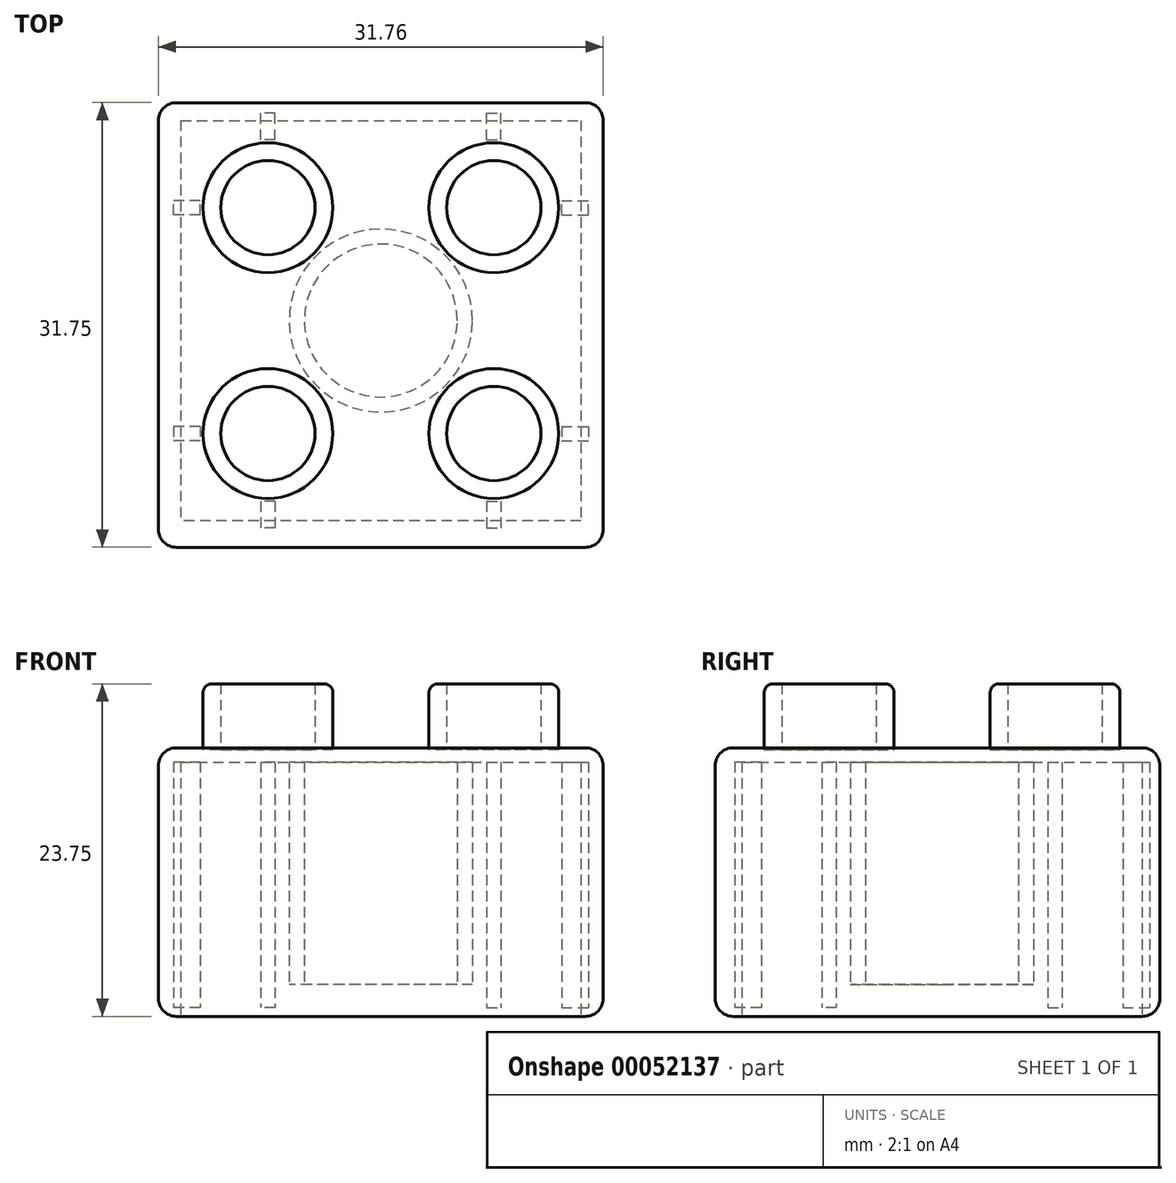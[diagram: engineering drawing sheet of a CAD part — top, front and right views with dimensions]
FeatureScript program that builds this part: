
annotation { "Feature Type Name" : "Feature", "Feature Type Description" : "" }
export const myFeature = defineFeature(function(context is Context, id is Id, definition is map)
    precondition{}
    {
        {
            var Q0;
            Q0=qCreatedBy(makeId("Top.planeOp"),FACE);
            var sketch = newSketch(context, id + "F0", { "sketchPlane" : qUnion([Q0])});
            skPoint(sketch, "E0", {"position": v(0, 16.87) * mm});
            skPoint(sketch, "E1", {"position": v(0, 15.88) * mm});
            skPoint(sketch, "E2", {"position": v(0, -14.88) * mm});
            skPoint(sketch, "E3", {"position": v(0, -15.88) * mm});
            skPoint(sketch, "E4", {"position": v(17.1, 0) * mm});
            skPoint(sketch, "E5", {"position": v(15.88, 0) * mm});
            skPoint(sketch, "E6", {"position": v(-15.88, 0) * mm});
            skPoint(sketch, "E7", {"position": v(15.64, 15.88) * mm});
            skPoint(sketch, "E8", {"position": v(15.88, 15.56) * mm});
            skPoint(sketch, "E9", {"position": v(-16.3, -15.88) * mm});
            skPoint(sketch, "E10", {"position": v(-15.88, -16.2) * mm});
            skLineSegment(sketch, "E11.bottom", {"start": v(-15.88, -16.2) * mm, "end": v(15.88, -16.2) * mm});
            skLineSegment(sketch, "E11.top", {"start": v(-15.88, 15.56) * mm, "end": v(15.88, 15.56) * mm});
            skLineSegment(sketch, "E11.left", {"start": v(-15.88, -16.2) * mm, "end": v(-15.88, 15.56) * mm});
            skLineSegment(sketch, "E11.right", {"start": v(15.88, -16.2) * mm, "end": v(15.88, 15.56) * mm});
            skSolve(sketch);
        }
        {
            var Q0;
            Q0=makeQuery(id+"F0.imprint","IMPRINT",FACE,{"disambiguationData":[TD([[makeQuery(id+"F0.imprint","IMPRINT",EDGE,{"derivedFrom":sQuery(id+"F0.wireOp",EDGE,"E11.bottom")}),1.0]])]});
            var sketch = newSketch(context, id + "F1", { "sketchPlane" : qUnion([Q0])});
            skPoint(sketch, "E12", {"position": v(14.77, 0) * mm});
            skPoint(sketch, "E13", {"position": v(14.29, 0) * mm});
            skPoint(sketch, "E14", {"position": v(-14.29, 0) * mm});
            skPoint(sketch, "E15", {"position": v(-14.29, -14.92) * mm});
            skPoint(sketch, "E16", {"position": v(-14.29, -14.29) * mm});
            skPoint(sketch, "E17", {"position": v(14.29, 14.33) * mm});
            skPoint(sketch, "E18", {"position": v(14.29, 14.29) * mm});
            skLineSegment(sketch, "E19.bottom", {"start": v(-14.29, -14.29) * mm, "end": v(14.29, -14.29) * mm});
            skLineSegment(sketch, "E19.top", {"start": v(-14.29, 14.29) * mm, "end": v(14.29, 14.29) * mm});
            skLineSegment(sketch, "E19.left", {"start": v(-14.29, -14.29) * mm, "end": v(-14.29, 14.29) * mm});
            skLineSegment(sketch, "E19.right", {"start": v(14.29, -14.29) * mm, "end": v(14.29, 14.29) * mm});
            skSolve(sketch);
        }
        {
            var Q0;
            Q0=makeQuery(id+"F1.imprint","IMPRINT",FACE,{"disambiguationData":[TD([[makeQuery(id+"F1.imprint","IMPRINT",EDGE,{"derivedFrom":sQuery(id+"F1.wireOp",EDGE,"E19.bottom")}),1.0]])]});
            var sketch = newSketch(context, id + "F2", { "sketchPlane" : qUnion([Q0])});
            skPoint(sketch, "E20", {"position": v(0, 0) * mm});
            skCircle(sketch, "E21", {"center": v(0, 0) * mm, "radius": 6.54 * mm});
            skSolve(sketch);
        }
        {
            var Q0;
            Q0=makeQuery(id+"F1.imprint","IMPRINT",FACE,{"disambiguationData":[TD([[makeQuery(id+"F1.imprint","IMPRINT",EDGE,{"derivedFrom":sQuery(id+"F1.wireOp",EDGE,"E19.bottom")}),1.0]])]});
            var sketch = newSketch(context, id + "F3", { "sketchPlane" : qUnion([Q0])});
            skPoint(sketch, "E22", {"position": v(0, 0) * mm});
            skCircle(sketch, "E23", {"center": v(0, 0) * mm, "radius": 5.46 * mm});
            skSolve(sketch);
        }
        {
            var Q0;
            Q0=makeQuery(id+"F1.imprint","IMPRINT",FACE,{"disambiguationData":[TD([[makeQuery(id+"F1.imprint","IMPRINT",EDGE,{"derivedFrom":sQuery(id+"F1.wireOp",EDGE,"E19.bottom")}),1.0]])]});
            var sketch = newSketch(context, id + "F4", { "sketchPlane" : qUnion([Q0])});
            skPoint(sketch, "E24", {"position": v(0, 1.02) * mm});
            skPoint(sketch, "E25", {"position": v(0, 0.95) * mm});
            skPoint(sketch, "E26", {"position": v(0, -0.95) * mm});
            skPoint(sketch, "E27", {"position": v(-0.23, 0) * mm});
            skPoint(sketch, "E28", {"position": v(-0.5, 0) * mm});
            skPoint(sketch, "E29", {"position": v(0.3, 0) * mm});
            skPoint(sketch, "E30", {"position": v(0.5, 0) * mm});
            skPoint(sketch, "E31", {"position": v(-0.5, -0.86) * mm});
            skPoint(sketch, "E32", {"position": v(-0.5, -0.95) * mm});
            skPoint(sketch, "E33", {"position": v(0.5, 0.95) * mm});
            skLineSegment(sketch, "E34.bottom", {"start": v(-0.5, -0.95) * mm, "end": v(0.5, -0.95) * mm});
            skLineSegment(sketch, "E34.top", {"start": v(-0.5, 0.95) * mm, "end": v(0.5, 0.95) * mm});
            skLineSegment(sketch, "E34.left", {"start": v(-0.5, -0.95) * mm, "end": v(-0.5, 0.95) * mm});
            skLineSegment(sketch, "E34.right", {"start": v(0.5, -0.95) * mm, "end": v(0.5, 0.95) * mm});
            skSolve(sketch);
        }
        {
            var Q0;
            Q0 = qSketchRegion(id + "F0", true);
            extrude(context, id + "F5", {"entities" : qUnion([Q0]), "depth" : 19.18 * mm});
        }
        {
            var Q0;
            Q0 = qSketchRegion(id + "F1", true);
            extrude(context, id + "F6", {"entities" : qUnion([Q0]), "operationType" : NewBodyOperationType.REMOVE, "depth" : 18.16 * mm, "hasSecondDirection" : true, "secondDirectionOppositeDirection" : true, "secondDirectionDepth" : 0.38 * mm});
        }
        {
            var Q0;
            Q0 = qSketchRegion(id + "F2", true);
            extrude(context, id + "F7", {"entities" : qUnion([Q0]), "operationType" : NewBodyOperationType.ADD, "depth" : 15.88 * mm});
        }
        {
            var Q0;
            Q0 = qSketchRegion(id + "F3", true);
            extrude(context, id + "F8", {"entities" : qUnion([Q0]), "operationType" : NewBodyOperationType.REMOVE, "depth" : 15.88 * mm, "hasSecondDirection" : true, "secondDirectionOppositeDirection" : true, "secondDirectionDepth" : 0.64 * mm});
        }
        {
            var Q0;
            Q0=makeQuery(id+"F7.opExtrude","SWEPT_BODY",BODY,{"disambiguationData":[OSD([sQuery(id+"F2.wireOp",EDGE,"E21")])]});
            transform(context, id + "F9", {"entities" : qUnion([Q0]), "transformType" : TransformType.TRANSLATION_3D, "dx" : 0 * mm, "dy" : 0 * mm, "dz" : 2.3 * mm, "makeCopy" : false});
        }
        {
            var Q0;
            Q0=makeQuery(id+"F4.imprint","IMPRINT",FACE,{"disambiguationData":[TD([[makeQuery(id+"F4.imprint","IMPRINT",EDGE,{"derivedFrom":sQuery(id+"F4.wireOp",EDGE,"E34.bottom")}),1.0]])]});
            extrude(context, id + "F10", {"entities" : qUnion([Q0]), "operationType" : NewBodyOperationType.ADD, "depth" : 17.53 * mm});
        }
        {
            var Q0;
            Q0=makeQuery(id+"F10.opExtrude","SWEPT_BODY",BODY,{"disambiguationData":[OSD([sQuery(id+"F4.wireOp",EDGE,"E34.bottom"),sQuery(id+"F4.wireOp",EDGE,"E34.top"),sQuery(id+"F4.wireOp",EDGE,"E34.left"),sQuery(id+"F4.wireOp",EDGE,"E34.right")])]});
            transform(context, id + "F11", {"entities" : qUnion([Q0]), "transformType" : TransformType.TRANSLATION_3D, "dx" : 8.06 * mm, "dy" : 13.86 * mm, "dz" : 0.64 * mm, "makeCopy" : false});
        }
        {
            var Q0;
            Q0=makeQuery(id+"F10.opExtrude","SWEPT_BODY",BODY,{"disambiguationData":[OSD([sQuery(id+"F4.wireOp",EDGE,"E34.bottom"),sQuery(id+"F4.wireOp",EDGE,"E34.top"),sQuery(id+"F4.wireOp",EDGE,"E34.left"),sQuery(id+"F4.wireOp",EDGE,"E34.right")])]});
            var Q1;
            Q1=qCreatedBy(makeId("Front.planeOp"),FACE);
            mirror(context, id + "F12", {"entities" : qUnion([Q0]), "mirrorPlane" : qUnion([Q1])});
        }
        {
            var Q0;
            Q0=makeQuery(id+"F12.opPattern","COPY",BODY,{"derivedFrom":makeQuery(id+"F10.opExtrude","SWEPT_BODY",BODY,{"disambiguationData":[OSD([sQuery(id+"F4.wireOp",EDGE,"E34.bottom"),sQuery(id+"F4.wireOp",EDGE,"E34.top"),sQuery(id+"F4.wireOp",EDGE,"E34.left"),sQuery(id+"F4.wireOp",EDGE,"E34.right")])]}),"instanceName":"1"});
            var Q1;
            Q1=makeQuery(id+"F10.opExtrude","SWEPT_BODY",BODY,{"disambiguationData":[OSD([sQuery(id+"F4.wireOp",EDGE,"E34.bottom"),sQuery(id+"F4.wireOp",EDGE,"E34.top"),sQuery(id+"F4.wireOp",EDGE,"E34.left"),sQuery(id+"F4.wireOp",EDGE,"E34.right")])]});
            var Q2;
            Q2=qCreatedBy(makeId("Right.planeOp"),FACE);
            mirror(context, id + "F13", {"entities" : qUnion([Q0, Q1]), "mirrorPlane" : qUnion([Q2])});
        }
        {
            var Q0;
            Q0=qCreatedBy(makeId("Front.planeOp"),FACE);
            var sketch = newSketch(context, id + "F14", { "sketchPlane" : qUnion([Q0])});
            skLineSegment(sketch, "E35", {"start": v(0, 40.9) * mm, "end": v(0, -32.36) * mm});
            skSolve(sketch);
        }
        {
            var Q0;
            Q0=makeQuery(id+"F12.opPattern","COPY",BODY,{"derivedFrom":makeQuery(id+"F10.opExtrude","SWEPT_BODY",BODY,{"disambiguationData":[OSD([sQuery(id+"F4.wireOp",EDGE,"E34.bottom"),sQuery(id+"F4.wireOp",EDGE,"E34.top"),sQuery(id+"F4.wireOp",EDGE,"E34.left"),sQuery(id+"F4.wireOp",EDGE,"E34.right")])]}),"instanceName":"1"});
            var Q1;
            Q1=makeQuery(id+"F13.opPattern","COPY",BODY,{"derivedFrom":makeQuery(id+"F12.opPattern","COPY",BODY,{"derivedFrom":makeQuery(id+"F10.opExtrude","SWEPT_BODY",BODY,{"disambiguationData":[OSD([sQuery(id+"F4.wireOp",EDGE,"E34.bottom"),sQuery(id+"F4.wireOp",EDGE,"E34.top"),sQuery(id+"F4.wireOp",EDGE,"E34.left"),sQuery(id+"F4.wireOp",EDGE,"E34.right")])]}),"instanceName":"1"}),"instanceName":"1"});
            var Q2;
            Q2=makeQuery(id+"F10.opExtrude","SWEPT_BODY",BODY,{"disambiguationData":[OSD([sQuery(id+"F4.wireOp",EDGE,"E34.bottom"),sQuery(id+"F4.wireOp",EDGE,"E34.top"),sQuery(id+"F4.wireOp",EDGE,"E34.left"),sQuery(id+"F4.wireOp",EDGE,"E34.right")])]});
            var Q3;
            Q3=makeQuery(id+"F13.opPattern","COPY",BODY,{"derivedFrom":makeQuery(id+"F10.opExtrude","SWEPT_BODY",BODY,{"disambiguationData":[OSD([sQuery(id+"F4.wireOp",EDGE,"E34.bottom"),sQuery(id+"F4.wireOp",EDGE,"E34.top"),sQuery(id+"F4.wireOp",EDGE,"E34.left"),sQuery(id+"F4.wireOp",EDGE,"E34.right")])]}),"instanceName":"1"});
            var Q4;
            Q4=sQuery(id+"F14.wireOp",EDGE,"E35");
            transform(context, id + "F15", {"entities" : qUnion([Q0, Q1, Q2, Q3]), "transformType" : TransformType.ROTATION, "transformAxis" : qUnion([Q4]), "angle" : 90 * degree, "makeCopy" : true});
        }
        {
            var Q0;
            Q0=qCreatedBy(makeId("Top.planeOp"),FACE);
            var sketch = newSketch(context, id + "F16", { "sketchPlane" : qUnion([Q0])});
            skCircle(sketch, "E36", {"center": v(0, 0) * mm, "radius": 4.64 * mm});
            skSolve(sketch);
        }
        {
            var Q0;
            Q0=qCreatedBy(makeId("Top.planeOp"),FACE);
            var sketch = newSketch(context, id + "F17", { "sketchPlane" : qUnion([Q0])});
            skCircle(sketch, "E37", {"center": v(0, 0) * mm, "radius": 3.37 * mm});
            skSolve(sketch);
        }
        {
            var Q0;
            Q0=makeQuery(id+"F16.imprint","IMPRINT",FACE,{"disambiguationData":[TD([[makeQuery(id+"F16.imprint","IMPRINT",EDGE,{"derivedFrom":sQuery(id+"F16.wireOp",EDGE,"E36")}),1.0]])]});
            extrude(context, id + "F18", {"entities" : qUnion([Q0]), "depth" : 4.7 * mm});
        }
        {
            var Q0;
            Q0=makeQuery(id+"F17.imprint","IMPRINT",FACE,{"disambiguationData":[TD([[makeQuery(id+"F17.imprint","IMPRINT",EDGE,{"derivedFrom":sQuery(id+"F17.wireOp",EDGE,"E37")}),1.0]])]});
            extrude(context, id + "F19", {"entities" : qUnion([Q0]), "operationType" : NewBodyOperationType.REMOVE, "depth" : 4.7 * mm});
        }
        {
            var Q0;
            Q0=makeQuery(id+"F18.opExtrude","SWEPT_BODY",BODY,{"disambiguationData":[OSD([sQuery(id+"F16.wireOp",EDGE,"E36")])]});
            transform(context, id + "F20", {"entities" : qUnion([Q0]), "transformType" : TransformType.TRANSLATION_3D, "dx" : 8.06 * mm, "dy" : 8.06 * mm, "dz" : 19.05 * mm, "makeCopy" : false});
        }
        {
            var Q0;
            Q0=makeQuery(id+"F18.opExtrude","SWEPT_BODY",BODY,{"disambiguationData":[OSD([sQuery(id+"F16.wireOp",EDGE,"E36")])]});
            var Q1;
            Q1=qCreatedBy(makeId("Front.planeOp"),FACE);
            mirror(context, id + "F21", {"entities" : qUnion([Q0]), "mirrorPlane" : qUnion([Q1])});
        }
        {
            var Q0;
            Q0=makeQuery(id+"F18.opExtrude","SWEPT_BODY",BODY,{"disambiguationData":[OSD([sQuery(id+"F16.wireOp",EDGE,"E36")])]});
            var Q1;
            Q1=makeQuery(id+"F21.opPattern","COPY",BODY,{"derivedFrom":makeQuery(id+"F18.opExtrude","SWEPT_BODY",BODY,{"disambiguationData":[OSD([sQuery(id+"F16.wireOp",EDGE,"E36")])]}),"instanceName":"1"});
            var Q2;
            Q2=qCreatedBy(makeId("Right.planeOp"),FACE);
            mirror(context, id + "F22", {"entities" : qUnion([Q0, Q1]), "mirrorPlane" : qUnion([Q2])});
        }
        {
            var Q0;
            Q0=makeQuery(id+"F5.opExtrude","CAP_EDGE",EDGE,{"disambiguationData":[OSD([sQuery(id+"F0.wireOp",EDGE,"E11.bottom")])],"isStart":false});
            var Q1;
            Q1=makeQuery(id+"F5.opExtrude","CAP_EDGE",EDGE,{"disambiguationData":[OSD([sQuery(id+"F0.wireOp",EDGE,"E11.left")])],"isStart":false});
            var Q2;
            Q2=makeQuery(id+"F5.opExtrude","CAP_EDGE",EDGE,{"disambiguationData":[OSD([sQuery(id+"F0.wireOp",EDGE,"E11.top")])],"isStart":false});
            var Q3;
            Q3=makeQuery(id+"F5.opExtrude","CAP_EDGE",EDGE,{"disambiguationData":[OSD([sQuery(id+"F0.wireOp",EDGE,"E11.right")])],"isStart":false});
            var Q4;
            Q4=makeQuery(id+"F5.opExtrude","SWEPT_EDGE",EDGE,{"disambiguationData":[OSD([sQuery(id+"F0.wireOp",EDGE,"E11.bottom"),sQuery(id+"F0.wireOp",EDGE,"E11.left")])]});
            var Q5;
            Q5=makeQuery(id+"F5.opExtrude","SWEPT_EDGE",EDGE,{"disambiguationData":[OSD([sQuery(id+"F0.wireOp",EDGE,"E11.bottom"),sQuery(id+"F0.wireOp",EDGE,"E11.right")])]});
            var Q6;
            Q6=makeQuery(id+"F5.opExtrude","SWEPT_EDGE",EDGE,{"disambiguationData":[OSD([sQuery(id+"F0.wireOp",EDGE,"E11.top"),sQuery(id+"F0.wireOp",EDGE,"E11.left")])]});
            var Q7;
            Q7=makeQuery(id+"F5.opExtrude","SWEPT_EDGE",EDGE,{"disambiguationData":[OSD([sQuery(id+"F0.wireOp",EDGE,"E11.top"),sQuery(id+"F0.wireOp",EDGE,"E11.right")])]});
            var Q8;
            Q8=makeQuery(id+"F5.opExtrude","CAP_EDGE",EDGE,{"disambiguationData":[OSD([sQuery(id+"F0.wireOp",EDGE,"E11.right")])],"isStart":true});
            var Q9;
            Q9=makeQuery(id+"F5.opExtrude","CAP_EDGE",EDGE,{"disambiguationData":[OSD([sQuery(id+"F0.wireOp",EDGE,"E11.bottom")])],"isStart":true});
            var Q10;
            Q10=makeQuery(id+"F5.opExtrude","CAP_EDGE",EDGE,{"disambiguationData":[OSD([sQuery(id+"F0.wireOp",EDGE,"E11.left")])],"isStart":true});
            var Q11;
            Q11=makeQuery(id+"F5.opExtrude","CAP_EDGE",EDGE,{"disambiguationData":[OSD([sQuery(id+"F0.wireOp",EDGE,"E11.top")])],"isStart":true});
            fillet(context, id + "F23", {"entities" : qUnion([Q0, Q1, Q2, Q3, Q4, Q5, Q6, Q7, Q8, Q9, Q10, Q11]), "radius" : 1.27 * mm, "tangentPropagation" : true, "allowEdgeOverflow" : false});
        }
        {
            var Q0;
            Q0=makeQuery(id+"F22.opPattern","COPY",EDGE,{"derivedFrom":makeQuery(id+"F18.opExtrude","CAP_EDGE",EDGE,{"disambiguationData":[OSD([sQuery(id+"F16.wireOp",EDGE,"E36")])],"isStart":false}),"instanceName":"1"});
            var Q1;
            Q1=makeQuery(id+"F18.opExtrude","CAP_EDGE",EDGE,{"disambiguationData":[OSD([sQuery(id+"F16.wireOp",EDGE,"E36")])],"isStart":false});
            var Q2;
            Q2=makeQuery(id+"F21.opPattern","COPY",EDGE,{"derivedFrom":makeQuery(id+"F18.opExtrude","CAP_EDGE",EDGE,{"disambiguationData":[OSD([sQuery(id+"F16.wireOp",EDGE,"E36")])],"isStart":false}),"instanceName":"1"});
            var Q3;
            Q3=makeQuery(id+"F22.opPattern","COPY",EDGE,{"derivedFrom":makeQuery(id+"F21.opPattern","COPY",EDGE,{"derivedFrom":makeQuery(id+"F18.opExtrude","CAP_EDGE",EDGE,{"disambiguationData":[OSD([sQuery(id+"F16.wireOp",EDGE,"E36")])],"isStart":false}),"instanceName":"1"}),"instanceName":"1"});
            fillet(context, id + "F24", {"entities" : qUnion([Q0, Q1, Q2, Q3]), "radius" : 0.64 * mm, "tangentPropagation" : true, "allowEdgeOverflow" : false});
        }
    });
